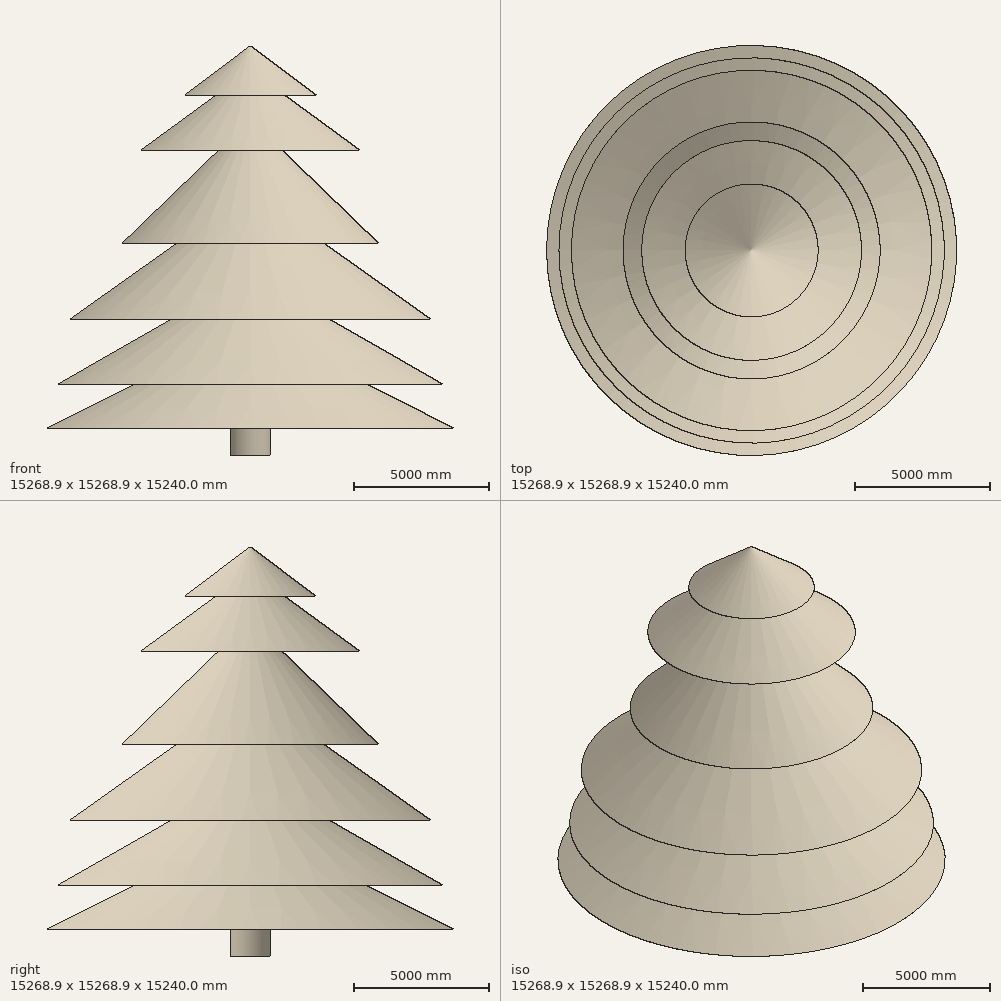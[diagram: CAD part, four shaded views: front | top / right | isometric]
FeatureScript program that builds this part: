
annotation { "Feature Type Name" : "Feature", "Feature Type Description" : "" }
export const myFeature = defineFeature(function(context is Context, id is Id, definition is map)
    precondition{}
    {
        {
            var Q0;
            Q0=qCreatedBy(makeId("Front.planeOp"),FACE);
            var sketch = newSketch(context, id + "F0", { "sketchPlane" : qUnion([Q0])});
            skLineSegment(sketch, "E0", {"start": v(0, 0) * mm, "end": v(0, 15240) * mm});
            skLineSegment(sketch, "E1", {"start": v(0, 15240) * mm, "end": v(2475.3, 13379.66) * mm});
            skLineSegment(sketch, "E2", {"start": v(2475.3, 13379.66) * mm, "end": v(511.75, 13957.18) * mm});
            skLineSegment(sketch, "E3", {"start": v(511.75, 13957.18) * mm, "end": v(4092.35, 11339.1) * mm});
            skLineSegment(sketch, "E4", {"start": v(4092.35, 11339.1) * mm, "end": v(473.25, 12032.13) * mm});
            skLineSegment(sketch, "E5", {"start": v(473.25, 12032.13) * mm, "end": v(4785.37, 7874.01) * mm});
            skLineSegment(sketch, "E6", {"start": v(4785.37, 7874.01) * mm, "end": v(1127.77, 9029.05) * mm});
            skLineSegment(sketch, "E7", {"start": v(1127.77, 9029.05) * mm, "end": v(6710.42, 5063.44) * mm});
            skLineSegment(sketch, "E8", {"start": v(6710.42, 5063.44) * mm, "end": v(1050.76, 6141.47) * mm});
            skLineSegment(sketch, "E9", {"start": v(1050.76, 6141.47) * mm, "end": v(7172.43, 2637.87) * mm});
            skLineSegment(sketch, "E10", {"start": v(7172.43, 2637.87) * mm, "end": v(1397.27, 4100.91) * mm});
            skLineSegment(sketch, "E11", {"start": v(1397.27, 4100.91) * mm, "end": v(7634.44, 982.32) * mm});
            skLineSegment(sketch, "E12", {"start": v(7634.44, 982.32) * mm, "end": v(757.58, 2292.2) * mm});
            skLineSegment(sketch, "E13", {"start": v(757.58, 2292.2) * mm, "end": v(757.58, 0) * mm});
            skLineSegment(sketch, "E14", {"start": v(757.58, 0) * mm, "end": v(0, 0) * mm});
            skSolve(sketch);
        }
        {
            var Q0;
            Q0=makeQuery(id+"F0.imprint","IMPRINT",FACE,{"disambiguationData":[TD([[makeQuery(id+"F0.imprint","IMPRINT",EDGE,{"derivedFrom":sQuery(id+"F0.wireOp",EDGE,"E0")}),-1.0]])]});
            var Q1;
            Q1=sQuery(id+"F0.wireOp",EDGE,"E0");
            revolve(context, id + "F1", {"entities" : qUnion([Q0]), "axis" : qUnion([Q1]), "revolveType" : RevolveType.FULL});
        }
    });
